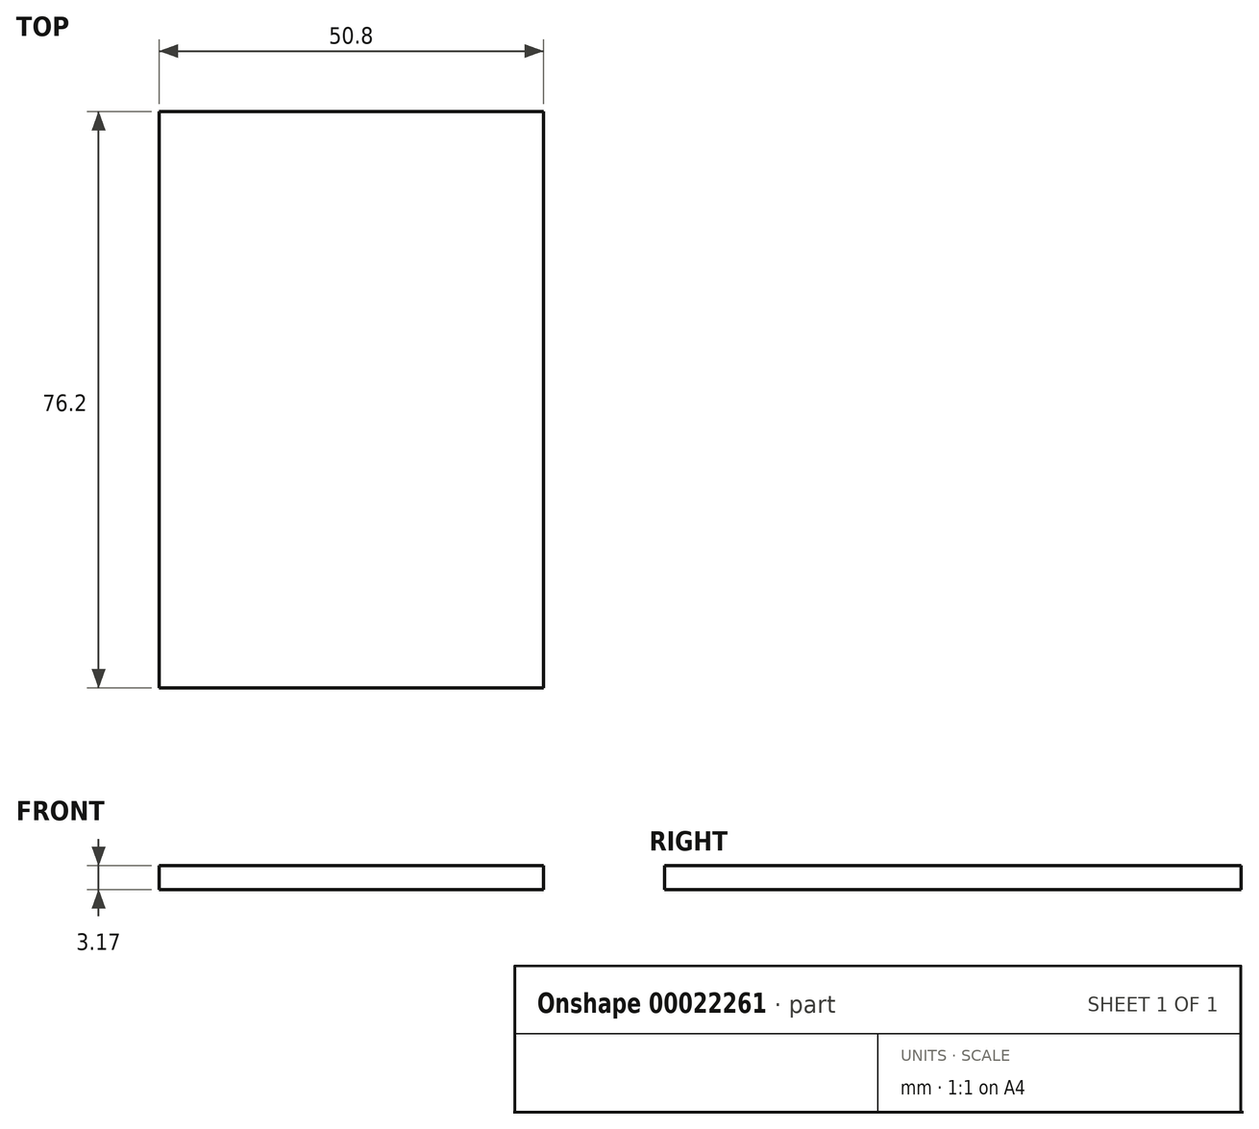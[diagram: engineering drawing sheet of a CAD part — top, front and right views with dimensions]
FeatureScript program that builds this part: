
annotation { "Feature Type Name" : "Feature", "Feature Type Description" : "" }
export const myFeature = defineFeature(function(context is Context, id is Id, definition is map)
    precondition{}
    {
        {
            var Q0;
            Q0=qCreatedBy(makeId("Top.planeOp"),FACE);
            var sketch = newSketch(context, id + "F0", { "sketchPlane" : qUnion([Q0])});
            skLineSegment(sketch, "E0.bottom", {"start": v(-25.4, 38.1) * mm, "end": v(25.4, 38.1) * mm});
            skLineSegment(sketch, "E0.top", {"start": v(-25.4, -38.1) * mm, "end": v(25.4, -38.1) * mm});
            skLineSegment(sketch, "E0.left", {"start": v(-25.4, 38.1) * mm, "end": v(-25.4, -38.1) * mm});
            skLineSegment(sketch, "E0.right", {"start": v(25.4, 38.1) * mm, "end": v(25.4, -38.1) * mm});
            skLineSegment(sketch, "E1", {"start": v(-25.4, 38.1) * mm, "end": v(25.4, -38.1) * mm, "construction": true});
            skSolve(sketch);
        }
        {
            var Q0;
            Q0 = qSketchRegion(id + "F0", true);
            extrude(context, id + "F1", {"entities" : qUnion([Q0]), "depth" : 3.17 * mm});
        }
    });
